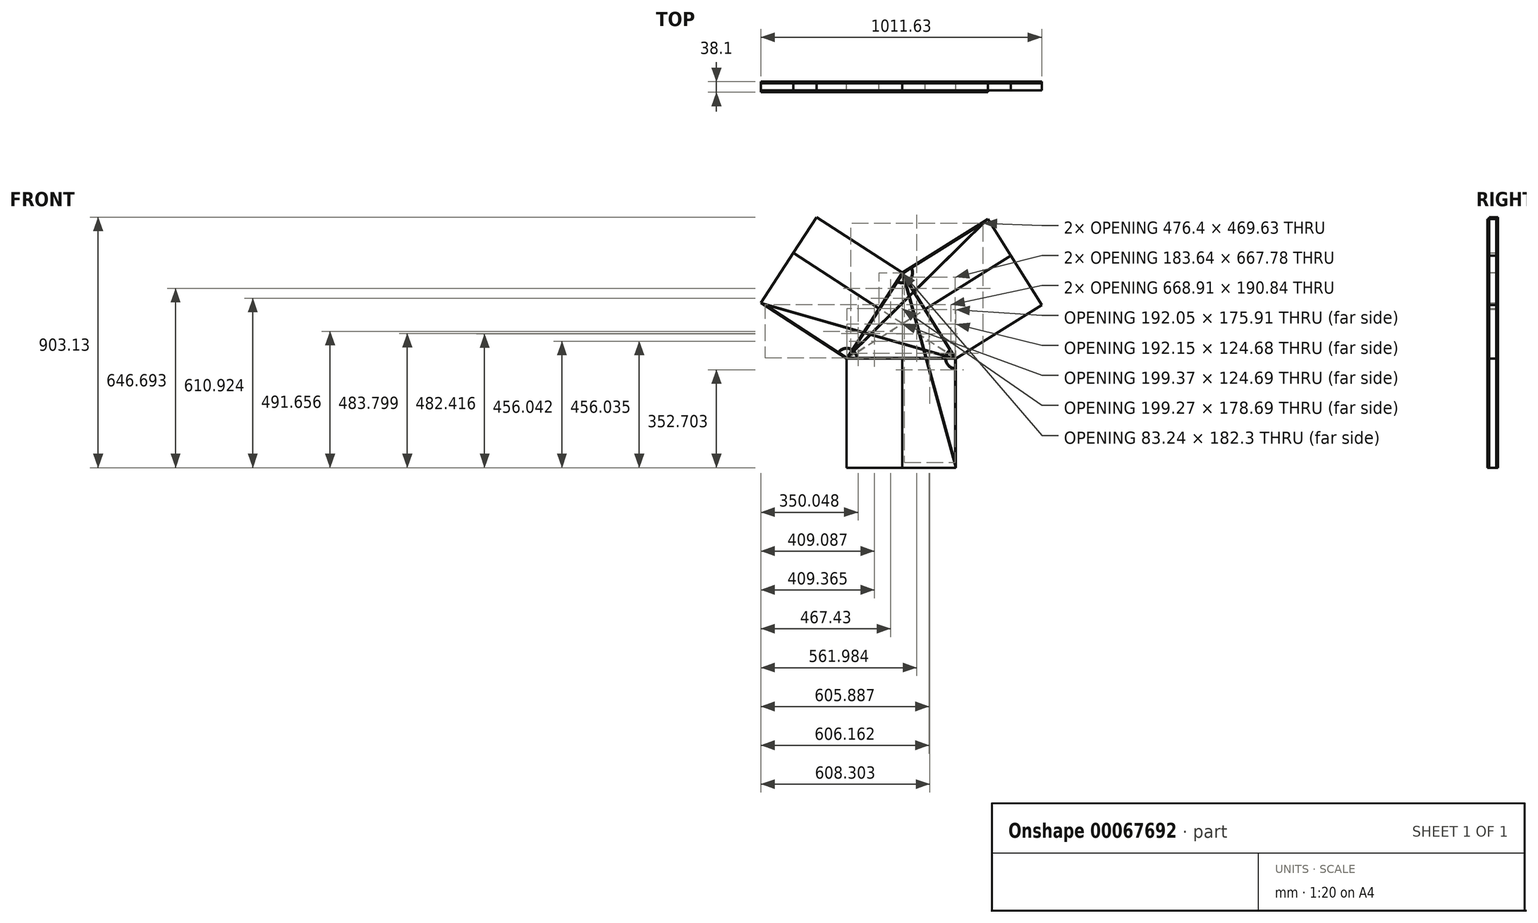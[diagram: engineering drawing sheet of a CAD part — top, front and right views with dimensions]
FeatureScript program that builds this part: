
annotation { "Feature Type Name" : "Feature", "Feature Type Description" : "" }
export const myFeature = defineFeature(function(context is Context, id is Id, definition is map)
    precondition{}
    {
        {
            var Q0;
            Q0=qCreatedBy(makeId("Front.planeOp"),FACE);
            var sketch = newSketch(context, id + "F0", { "sketchPlane" : qUnion([Q0])});
            skLineSegment(sketch, "E0", {"start": v(0, 0) * mm, "end": v(-200.47, -308.96) * mm});
            skLineSegment(sketch, "E1", {"start": v(-200.47, -308.96) * mm, "end": v(193.23, -308.96) * mm});
            skLineSegment(sketch, "E2", {"start": v(193.23, -308.96) * mm, "end": v(0, 0) * mm});
            skLineSegment(sketch, "E3", {"start": v(-200.47, -308.96) * mm, "end": v(82.53, -131.97) * mm});
            skLineSegment(sketch, "E4", {"start": v(193.23, -308.96) * mm, "end": v(-83.83, -129.2) * mm});
            skLineSegment(sketch, "E5", {"start": v(0, 0) * mm, "end": v(0, -308.96) * mm});
            skLineSegment(sketch, "E6", {"start": v(0, 0) * mm, "end": v(308.96, 193.23) * mm});
            skLineSegment(sketch, "E7", {"start": v(308.96, 193.23) * mm, "end": v(502.2, -115.73) * mm});
            skLineSegment(sketch, "E8", {"start": v(502.2, -115.73) * mm, "end": v(193.23, -308.96) * mm});
            skLineSegment(sketch, "E9", {"start": v(82.53, -131.97) * mm, "end": v(391.5, 61.27) * mm});
            skLineSegment(sketch, "E10", {"start": v(0, 0) * mm, "end": v(-308.96, 200.47) * mm});
            skLineSegment(sketch, "E11", {"start": v(-308.96, 200.47) * mm, "end": v(-509.43, -108.5) * mm});
            skLineSegment(sketch, "E12", {"start": v(-509.43, -108.5) * mm, "end": v(-200.47, -308.96) * mm});
            skLineSegment(sketch, "E13", {"start": v(-83.83, -129.2) * mm, "end": v(-392.79, 71.27) * mm});
            skLineSegment(sketch, "E14", {"start": v(-200.47, -308.96) * mm, "end": v(-200.47, -702.66) * mm});
            skLineSegment(sketch, "E15", {"start": v(-200.47, -702.66) * mm, "end": v(193.23, -702.66) * mm});
            skLineSegment(sketch, "E16", {"start": v(193.23, -702.66) * mm, "end": v(193.23, -308.96) * mm});
            skLineSegment(sketch, "E17", {"start": v(0, -308.96) * mm, "end": v(0, -702.66) * mm});
            skSolve(sketch);
        }
        {
            var Q0;
            {var subQ0=sQuery(id+"F0.wireOp",EDGE,"E10");Q0=makeQuery(id+"F0.imprint","IMPRINT",FACE,{"disambiguationData":[TD([[makeQuery(id+"F0.imprint","IMPRINT",EDGE,{"derivedFrom":subQ0}),1.0]])]});}
            var Q1;
            {var subQ0=sQuery(id+"F0.wireOp",EDGE,"E12");Q1=makeQuery(id+"F0.imprint","IMPRINT",FACE,{"disambiguationData":[TD([[makeQuery(id+"F0.imprint","IMPRINT",EDGE,{"derivedFrom":subQ0}),1.0]])]});}
            var Q2;
            {var subQ0=sQuery(id+"F0.wireOp",EDGE,"E14");Q2=makeQuery(id+"F0.imprint","IMPRINT",FACE,{"disambiguationData":[TD([[makeQuery(id+"F0.imprint","IMPRINT",EDGE,{"derivedFrom":subQ0}),1.0]])]});}
            var Q3;
            {var subQ0=sQuery(id+"F0.wireOp",EDGE,"E16");Q3=makeQuery(id+"F0.imprint","IMPRINT",FACE,{"disambiguationData":[TD([[makeQuery(id+"F0.imprint","IMPRINT",EDGE,{"derivedFrom":subQ0}),1.0]])]});}
            var Q4;
            {var subQ0=sQuery(id+"F0.wireOp",EDGE,"E8");Q4=makeQuery(id+"F0.imprint","IMPRINT",FACE,{"disambiguationData":[TD([[makeQuery(id+"F0.imprint","IMPRINT",EDGE,{"derivedFrom":subQ0}),-1.0]])]});}
            var Q5;
            {var subQ0=sQuery(id+"F0.wireOp",EDGE,"E6");Q5=makeQuery(id+"F0.imprint","IMPRINT",FACE,{"disambiguationData":[TD([[makeQuery(id+"F0.imprint","IMPRINT",EDGE,{"derivedFrom":subQ0}),-1.0]])]});}
            var Q6;
            {var subQ1=sQuery(id+"F0.wireOp",EDGE,"E2");var subQ3=sQuery(id+"F0.wireOp",EDGE,"E3");var subQ4=makeQuery(id+"F0.imprint","INTERSECT",VERTEX,{"derivedFrom":[subQ1,subQ3,sQuery(id+"F0.wireOp",EDGE,"E9")]});Q6=makeQuery(id+"F0.imprint","IMPRINT",FACE,{"disambiguationData":[TD([[makeQuery(id+"F0.imprint","IMPRINT",EDGE,{"disambiguationData":[TD([[subQ4,1.0]])],"derivedFrom":subQ3}),-1.0]])]});}
            var Q7;
            {var subQ1=sQuery(id+"F0.wireOp",EDGE,"E2");var subQ3=sQuery(id+"F0.wireOp",EDGE,"E3");var subQ4=makeQuery(id+"F0.imprint","INTERSECT",VERTEX,{"derivedFrom":[subQ1,subQ3,sQuery(id+"F0.wireOp",EDGE,"E9")]});Q7=makeQuery(id+"F0.imprint","IMPRINT",FACE,{"disambiguationData":[TD([[makeQuery(id+"F0.imprint","IMPRINT",EDGE,{"disambiguationData":[TD([[subQ4,1.0]])],"derivedFrom":subQ3}),1.0]])]});}
            var Q8;
            {var subQ1=sQuery(id+"F0.wireOp",EDGE,"E0");var subQ3=sQuery(id+"F0.wireOp",EDGE,"E4");var subQ4=makeQuery(id+"F0.imprint","INTERSECT",VERTEX,{"derivedFrom":[subQ1,subQ3,sQuery(id+"F0.wireOp",EDGE,"E13")]});Q8=makeQuery(id+"F0.imprint","IMPRINT",FACE,{"disambiguationData":[TD([[makeQuery(id+"F0.imprint","IMPRINT",EDGE,{"disambiguationData":[TD([[subQ4,1.0]])],"derivedFrom":subQ3}),-1.0]])]});}
            var Q9;
            {var subQ1=sQuery(id+"F0.wireOp",EDGE,"E0");var subQ3=sQuery(id+"F0.wireOp",EDGE,"E4");var subQ4=makeQuery(id+"F0.imprint","INTERSECT",VERTEX,{"derivedFrom":[subQ1,subQ3,sQuery(id+"F0.wireOp",EDGE,"E13")]});Q9=makeQuery(id+"F0.imprint","IMPRINT",FACE,{"disambiguationData":[TD([[makeQuery(id+"F0.imprint","IMPRINT",EDGE,{"disambiguationData":[TD([[subQ4,1.0]])],"derivedFrom":subQ3}),1.0]])]});}
            var Q10;
            {var subQ1=sQuery(id+"F0.wireOp",EDGE,"E1");var subQ3=sQuery(id+"F0.wireOp",EDGE,"E5");var subQ4=makeQuery(id+"F0.imprint","INTERSECT",VERTEX,{"derivedFrom":[subQ1,subQ3,sQuery(id+"F0.wireOp",EDGE,"E17")]});Q10=makeQuery(id+"F0.imprint","IMPRINT",FACE,{"disambiguationData":[TD([[makeQuery(id+"F0.imprint","IMPRINT",EDGE,{"disambiguationData":[TD([[subQ4,1.0]])],"derivedFrom":subQ3}),-1.0]])]});}
            var Q11;
            {var subQ1=sQuery(id+"F0.wireOp",EDGE,"E1");var subQ3=sQuery(id+"F0.wireOp",EDGE,"E5");var subQ4=makeQuery(id+"F0.imprint","INTERSECT",VERTEX,{"derivedFrom":[subQ1,subQ3,sQuery(id+"F0.wireOp",EDGE,"E17")]});Q11=makeQuery(id+"F0.imprint","IMPRINT",FACE,{"disambiguationData":[TD([[makeQuery(id+"F0.imprint","IMPRINT",EDGE,{"disambiguationData":[TD([[subQ4,1.0]])],"derivedFrom":subQ3}),1.0]])]});}
            extrude(context, id + "F1", {"entities" : qUnion([Q0, Q1, Q2, Q3, Q4, Q5, Q6, Q7, Q8, Q9, Q10, Q11]), "oppositeDirection" : true, "depth" : 6.35 * mm});
        }
        {
            var Q0;
            Q0=makeQuery(id+"F1.opExtrude","CAP_FACE",FACE,{"disambiguationData":[OSD([sQuery(id+"F0.wireOp",EDGE,"E6"),sQuery(id+"F0.wireOp",EDGE,"E7"),sQuery(id+"F0.wireOp",EDGE,"E8"),sQuery(id+"F0.wireOp",EDGE,"E10"),sQuery(id+"F0.wireOp",EDGE,"E11"),sQuery(id+"F0.wireOp",EDGE,"E12"),sQuery(id+"F0.wireOp",EDGE,"E14"),sQuery(id+"F0.wireOp",EDGE,"E15"),sQuery(id+"F0.wireOp",EDGE,"E16")])],"isStart":true});
            var sketch = newSketch(context, id + "F2", { "sketchPlane" : qUnion([Q0])});
            skLineSegment(sketch, "E18", {"start": v(0, 0) * mm, "end": v(0, -702.66) * mm});
            skLineSegment(sketch, "E19", {"start": v(193.23, -308.96) * mm, "end": v(-392.79, 71.27) * mm});
            skLineSegment(sketch, "E20", {"start": v(-200.47, -308.96) * mm, "end": v(391.5, 61.27) * mm});
            skPoint(sketch, "E20.endSnap0", {"position": v(405.58, 38.75) * mm});
            skArc(sketch, "E21.0.startCap", {"start": v(-0.38, 0) * mm, "mid": v(0, 0.38) * mm, "end": v(0.38, 0) * mm});
            skArc(sketch, "E21.0.endCap", {"start": v(0.38, -702.66) * mm, "mid": v(0, -703.04) * mm, "end": v(-0.38, -702.66) * mm});
            skLineSegment(sketch, "E21.0.left", {"start": v(0.38, 0) * mm, "end": v(0.38, -702.66) * mm});
            skLineSegment(sketch, "E21.0.right", {"start": v(-0.38, 0) * mm, "end": v(-0.38, -702.66) * mm});
            skArc(sketch, "E21.1.startCap", {"start": v(-200.27, -309.29) * mm, "mid": v(-200.8, -309.16) * mm, "end": v(-200.67, -308.64) * mm});
            skArc(sketch, "E21.1.endCap", {"start": v(391.3, 61.59) * mm, "mid": v(391.82, 61.47) * mm, "end": v(391.7, 60.94) * mm});
            skLineSegment(sketch, "E21.1.left", {"start": v(-200.67, -308.64) * mm, "end": v(391.3, 61.59) * mm});
            skLineSegment(sketch, "E21.1.right", {"start": v(-200.27, -309.29) * mm, "end": v(391.7, 60.94) * mm});
            skArc(sketch, "E21.2.startCap", {"start": v(193.44, -308.64) * mm, "mid": v(193.55, -309.17) * mm, "end": v(193.03, -309.28) * mm});
            skArc(sketch, "E21.2.endCap", {"start": v(-393, 70.95) * mm, "mid": v(-393.1, 71.48) * mm, "end": v(-392.58, 71.6) * mm});
            skLineSegment(sketch, "E21.2.left", {"start": v(193.03, -309.28) * mm, "end": v(-393, 70.95) * mm});
            skLineSegment(sketch, "E21.2.right", {"start": v(193.44, -308.64) * mm, "end": v(-392.58, 71.6) * mm});
            skSolve(sketch);
        }
        {
            var Q0;
            Q0=makeQuery(id+"F1.opExtrude","CAP_FACE",FACE,{"disambiguationData":[OSD([sQuery(id+"F0.wireOp",EDGE,"E6"),sQuery(id+"F0.wireOp",EDGE,"E7"),sQuery(id+"F0.wireOp",EDGE,"E8"),sQuery(id+"F0.wireOp",EDGE,"E10"),sQuery(id+"F0.wireOp",EDGE,"E11"),sQuery(id+"F0.wireOp",EDGE,"E12"),sQuery(id+"F0.wireOp",EDGE,"E14"),sQuery(id+"F0.wireOp",EDGE,"E15"),sQuery(id+"F0.wireOp",EDGE,"E16")])],"isStart":true});
            var sketch = newSketch(context, id + "F3", { "sketchPlane" : qUnion([Q0])});
            skLineSegment(sketch, "E22", {"start": v(0, 0) * mm, "end": v(-200.47, -308.96) * mm});
            skLineSegment(sketch, "E23", {"start": v(-200.47, -308.96) * mm, "end": v(193.23, -308.96) * mm});
            skLineSegment(sketch, "E24", {"start": v(193.23, -308.96) * mm, "end": v(0, 0) * mm});
            skArc(sketch, "E25.0.startCap", {"start": v(-0.32, 0.2) * mm, "mid": v(0.2, 0.32) * mm, "end": v(0.32, -0.2) * mm});
            skArc(sketch, "E25.0.endCap", {"start": v(-200.15, -309.17) * mm, "mid": v(-200.67, -309.28) * mm, "end": v(-200.79, -308.76) * mm});
            skLineSegment(sketch, "E25.0.left", {"start": v(0.32, -0.2) * mm, "end": v(-200.15, -309.17) * mm});
            skLineSegment(sketch, "E25.0.right", {"start": v(-0.32, 0.2) * mm, "end": v(-200.79, -308.76) * mm});
            skArc(sketch, "E25.1.startCap", {"start": v(-200.47, -309.34) * mm, "mid": v(-200.85, -308.96) * mm, "end": v(-200.47, -308.58) * mm});
            skArc(sketch, "E25.1.endCap", {"start": v(193.23, -308.58) * mm, "mid": v(193.61, -308.96) * mm, "end": v(193.23, -309.34) * mm});
            skLineSegment(sketch, "E25.1.left", {"start": v(-200.47, -308.58) * mm, "end": v(193.23, -308.58) * mm});
            skLineSegment(sketch, "E25.1.right", {"start": v(-200.47, -309.34) * mm, "end": v(193.23, -309.34) * mm});
            skArc(sketch, "E25.2.startCap", {"start": v(193.56, -308.76) * mm, "mid": v(193.43, -309.29) * mm, "end": v(192.9, -309.16) * mm});
            skArc(sketch, "E25.2.endCap", {"start": v(-0.32, -0.2) * mm, "mid": v(-0.2, 0.32) * mm, "end": v(0.32, 0.2) * mm});
            skLineSegment(sketch, "E25.2.left", {"start": v(192.9, -309.16) * mm, "end": v(-0.32, -0.2) * mm});
            skLineSegment(sketch, "E25.2.right", {"start": v(193.56, -308.76) * mm, "end": v(0.32, 0.2) * mm});
            skSolve(sketch);
        }
        {
            var Q0;
            Q0 = qSketchRegion(id + "F2", true);
            var Q1;
            Q1 = qSketchRegion(id + "F3", true);
            extrude(context, id + "F4", {"entities" : qUnion([Q0, Q1]), "operationType" : NewBodyOperationType.REMOVE, "oppositeDirection" : true, "depth" : 0.76 * mm});
        }
        {
            var Q0;
            {var subQ0=sQuery(id+"F0.wireOp",EDGE,"E12");Q0=makeQuery(id+"F0.imprint","IMPRINT",FACE,{"disambiguationData":[TD([[makeQuery(id+"F0.imprint","IMPRINT",EDGE,{"derivedFrom":subQ0}),1.0]])]});}
            var Q1;
            {var subQ0=sQuery(id+"F0.wireOp",EDGE,"E14");Q1=makeQuery(id+"F0.imprint","IMPRINT",FACE,{"disambiguationData":[TD([[makeQuery(id+"F0.imprint","IMPRINT",EDGE,{"derivedFrom":subQ0}),1.0]])]});}
            extrude(context, id + "F5", {"entities" : qUnion([Q0, Q1]), "depth" : 25.4 * mm});
        }
        {
            var Q0;
            {var subQ0=sQuery(id+"F0.wireOp",EDGE,"E8");Q0=makeQuery(id+"F0.imprint","IMPRINT",FACE,{"disambiguationData":[TD([[makeQuery(id+"F0.imprint","IMPRINT",EDGE,{"derivedFrom":subQ0}),-1.0]])]});}
            var Q1;
            {var subQ0=sQuery(id+"F0.wireOp",EDGE,"E16");Q1=makeQuery(id+"F0.imprint","IMPRINT",FACE,{"disambiguationData":[TD([[makeQuery(id+"F0.imprint","IMPRINT",EDGE,{"derivedFrom":subQ0}),1.0]])]});}
            extrude(context, id + "F6", {"entities" : qUnion([Q0, Q1]), "depth" : 25.4 * mm});
        }
        {
            var Q0;
            {var subQ0=sQuery(id+"F0.wireOp",EDGE,"E6");Q0=makeQuery(id+"F0.imprint","IMPRINT",FACE,{"disambiguationData":[TD([[makeQuery(id+"F0.imprint","IMPRINT",EDGE,{"derivedFrom":subQ0}),-1.0]])]});}
            var Q1;
            {var subQ0=sQuery(id+"F0.wireOp",EDGE,"E10");Q1=makeQuery(id+"F0.imprint","IMPRINT",FACE,{"disambiguationData":[TD([[makeQuery(id+"F0.imprint","IMPRINT",EDGE,{"derivedFrom":subQ0}),1.0]])]});}
            extrude(context, id + "F7", {"entities" : qUnion([Q0, Q1]), "depth" : 25.4 * mm});
        }
        {
            var Q0;
            {var subQ1=sQuery(id+"F0.wireOp",EDGE,"E1");var subQ3=sQuery(id+"F0.wireOp",EDGE,"E5");var subQ4=makeQuery(id+"F0.imprint","INTERSECT",VERTEX,{"derivedFrom":[subQ1,subQ3,sQuery(id+"F0.wireOp",EDGE,"E17")]});Q0=makeQuery(id+"F0.imprint","IMPRINT",FACE,{"disambiguationData":[TD([[makeQuery(id+"F0.imprint","IMPRINT",EDGE,{"disambiguationData":[TD([[subQ4,1.0]])],"derivedFrom":subQ3}),-1.0]])]});}
            var Q1;
            {var subQ1=sQuery(id+"F0.wireOp",EDGE,"E0");var subQ3=sQuery(id+"F0.wireOp",EDGE,"E4");var subQ4=makeQuery(id+"F0.imprint","INTERSECT",VERTEX,{"derivedFrom":[subQ1,subQ3,sQuery(id+"F0.wireOp",EDGE,"E13")]});Q1=makeQuery(id+"F0.imprint","IMPRINT",FACE,{"disambiguationData":[TD([[makeQuery(id+"F0.imprint","IMPRINT",EDGE,{"disambiguationData":[TD([[subQ4,1.0]])],"derivedFrom":subQ3}),1.0]])]});}
            var Q2;
            {var subQ1=sQuery(id+"F0.wireOp",EDGE,"E0");var subQ3=sQuery(id+"F0.wireOp",EDGE,"E4");var subQ4=makeQuery(id+"F0.imprint","INTERSECT",VERTEX,{"derivedFrom":[subQ1,subQ3,sQuery(id+"F0.wireOp",EDGE,"E13")]});Q2=makeQuery(id+"F0.imprint","IMPRINT",FACE,{"disambiguationData":[TD([[makeQuery(id+"F0.imprint","IMPRINT",EDGE,{"disambiguationData":[TD([[subQ4,1.0]])],"derivedFrom":subQ3}),-1.0]])]});}
            var Q3;
            {var subQ1=sQuery(id+"F0.wireOp",EDGE,"E2");var subQ3=sQuery(id+"F0.wireOp",EDGE,"E3");var subQ4=makeQuery(id+"F0.imprint","INTERSECT",VERTEX,{"derivedFrom":[subQ1,subQ3,sQuery(id+"F0.wireOp",EDGE,"E9")]});Q3=makeQuery(id+"F0.imprint","IMPRINT",FACE,{"disambiguationData":[TD([[makeQuery(id+"F0.imprint","IMPRINT",EDGE,{"disambiguationData":[TD([[subQ4,1.0]])],"derivedFrom":subQ3}),1.0]])]});}
            var Q4;
            {var subQ1=sQuery(id+"F0.wireOp",EDGE,"E2");var subQ3=sQuery(id+"F0.wireOp",EDGE,"E3");var subQ4=makeQuery(id+"F0.imprint","INTERSECT",VERTEX,{"derivedFrom":[subQ1,subQ3,sQuery(id+"F0.wireOp",EDGE,"E9")]});Q4=makeQuery(id+"F0.imprint","IMPRINT",FACE,{"disambiguationData":[TD([[makeQuery(id+"F0.imprint","IMPRINT",EDGE,{"disambiguationData":[TD([[subQ4,1.0]])],"derivedFrom":subQ3}),-1.0]])]});}
            var Q5;
            {var subQ1=sQuery(id+"F0.wireOp",EDGE,"E1");var subQ3=sQuery(id+"F0.wireOp",EDGE,"E5");var subQ4=makeQuery(id+"F0.imprint","INTERSECT",VERTEX,{"derivedFrom":[subQ1,subQ3,sQuery(id+"F0.wireOp",EDGE,"E17")]});Q5=makeQuery(id+"F0.imprint","IMPRINT",FACE,{"disambiguationData":[TD([[makeQuery(id+"F0.imprint","IMPRINT",EDGE,{"disambiguationData":[TD([[subQ4,1.0]])],"derivedFrom":subQ3}),1.0]])]});}
            extrude(context, id + "F8", {"entities" : qUnion([Q0, Q1, Q2, Q3, Q4, Q5]), "depth" : 25.4 * mm});
        }
        {
            var Q0;
            Q0=makeQuery(id+"F8.opExtrude","CAP_FACE",FACE,{"disambiguationData":[OSD([sQuery(id+"F0.wireOp",EDGE,"E0"),sQuery(id+"F0.wireOp",EDGE,"E1"),sQuery(id+"F0.wireOp",EDGE,"E2")])],"isStart":false});
            var sketch = newSketch(context, id + "F9", { "sketchPlane" : qUnion([Q0])});
            skLineSegment(sketch, "E26", {"start": v(-200.47, -308.96) * mm, "end": v(-509.43, -108.5) * mm});
            skLineSegment(sketch, "E27", {"start": v(-509.43, -108.5) * mm, "end": v(193.23, -308.96) * mm});
            skLineSegment(sketch, "E28", {"start": v(193.23, -308.96) * mm, "end": v(-200.47, -308.96) * mm});
            skArc(sketch, "E29", {"start": v(-230.98, -286.14) * mm, "mid": v(-189.65, -272.43) * mm, "end": v(-162.45, -306.42) * mm});
            skLineSegment(sketch, "E30.0", {"start": v(-493.84, -115.59) * mm, "end": v(175.07, -306.42) * mm});
            skLineSegment(sketch, "E30.1", {"start": v(-493.84, -115.59) * mm, "end": v(-230.98, -286.14) * mm});
            skLineSegment(sketch, "E30.2", {"start": v(-199.72, -306.42) * mm, "end": v(-165, -306.42) * mm});
            skArc(sketch, "E31.0", {"start": v(-228.84, -287.53) * mm, "mid": v(-190.37, -274.86) * mm, "end": v(-165, -306.42) * mm});
            skLineSegment(sketch, "E32.trimOffspring", {"start": v(-228.84, -287.53) * mm, "end": v(-199.72, -306.42) * mm});
            skLineSegment(sketch, "E33.trimOffspring", {"start": v(-162.45, -306.42) * mm, "end": v(175.07, -306.42) * mm});
            skSolve(sketch);
        }
        {
            var Q0;
            Q0 = qSketchRegion(id + "F9", true);
            extrude(context, id + "F10", {"entities" : qUnion([Q0]), "depth" : 6.35 * mm});
        }
        {
            var Q0;
            Q0=makeQuery(id+"F8.opExtrude","CAP_FACE",FACE,{"disambiguationData":[OSD([sQuery(id+"F0.wireOp",EDGE,"E0"),sQuery(id+"F0.wireOp",EDGE,"E1"),sQuery(id+"F0.wireOp",EDGE,"E2")])],"isStart":false});
            var sketch = newSketch(context, id + "F11", { "sketchPlane" : qUnion([Q0])});
            skLineSegment(sketch, "E34", {"start": v(0, 0) * mm, "end": v(193.23, -702.66) * mm});
            skLineSegment(sketch, "E35", {"start": v(193.23, -702.66) * mm, "end": v(193.23, -308.96) * mm});
            skLineSegment(sketch, "E36", {"start": v(193.23, -308.96) * mm, "end": v(0, 0) * mm});
            skArc(sketch, "E37", {"start": v(170.92, -278.08) * mm, "mid": v(156.61, -319.47) * mm, "end": v(190.7, -346.98) * mm});
            skLineSegment(sketch, "E38.0", {"start": v(7.05, -16.07) * mm, "end": v(190.7, -683.85) * mm});
            skLineSegment(sketch, "E38.1", {"start": v(190.7, -309.7) * mm, "end": v(172.27, -280.24) * mm});
            skLineSegment(sketch, "E38.2", {"start": v(190.7, -683.85) * mm, "end": v(190.7, -346.98) * mm});
            skArc(sketch, "E39.0", {"start": v(172.27, -280.24) * mm, "mid": v(159.05, -318.77) * mm, "end": v(190.7, -344.43) * mm});
            skLineSegment(sketch, "E40.trimOffspring", {"start": v(170.92, -278.08) * mm, "end": v(7.05, -16.07) * mm});
            skLineSegment(sketch, "E41.trimOffspring", {"start": v(190.7, -344.43) * mm, "end": v(190.7, -309.7) * mm});
            skSolve(sketch);
        }
        {
            var Q0;
            Q0 = qSketchRegion(id + "F11", true);
            extrude(context, id + "F12", {"entities" : qUnion([Q0]), "depth" : 6.35 * mm});
        }
        {
            var Q0;
            Q0=makeQuery(id+"F8.opExtrude","CAP_FACE",FACE,{"disambiguationData":[OSD([sQuery(id+"F0.wireOp",EDGE,"E0"),sQuery(id+"F0.wireOp",EDGE,"E1"),sQuery(id+"F0.wireOp",EDGE,"E2")])],"isStart":false});
            var sketch = newSketch(context, id + "F13", { "sketchPlane" : qUnion([Q0])});
            skLineSegment(sketch, "E42", {"start": v(0, 0) * mm, "end": v(308.96, 193.23) * mm});
            skLineSegment(sketch, "E43", {"start": v(308.96, 193.23) * mm, "end": v(-200.47, -308.96) * mm});
            skLineSegment(sketch, "E44", {"start": v(-200.47, -308.96) * mm, "end": v(0, 0) * mm});
            skArc(sketch, "E45", {"start": v(33.58, 18) * mm, "mid": v(26.72, -27.16) * mm, "end": v(-18.56, -33.27) * mm});
            skLineSegment(sketch, "E46.0", {"start": v(1.82, -1.85) * mm, "end": v(31.42, 16.65) * mm});
            skLineSegment(sketch, "E46.1", {"start": v(-185.64, -290.78) * mm, "end": v(-18.56, -33.27) * mm});
            skLineSegment(sketch, "E46.2", {"start": v(290.75, 178.85) * mm, "end": v(-185.64, -290.78) * mm});
            skArc(sketch, "E47.0", {"start": v(31.42, 16.65) * mm, "mid": v(24.93, -25.35) * mm, "end": v(-17.18, -31.14) * mm});
            skLineSegment(sketch, "E48.trimOffspring", {"start": v(33.58, 18) * mm, "end": v(290.75, 178.85) * mm});
            skLineSegment(sketch, "E49.trimOffspring", {"start": v(-17.18, -31.14) * mm, "end": v(1.82, -1.85) * mm});
            skSolve(sketch);
        }
        {
            var Q0;
            Q0 = qSketchRegion(id + "F13", true);
            extrude(context, id + "F14", {"entities" : qUnion([Q0]), "depth" : 6.35 * mm});
        }
    });
